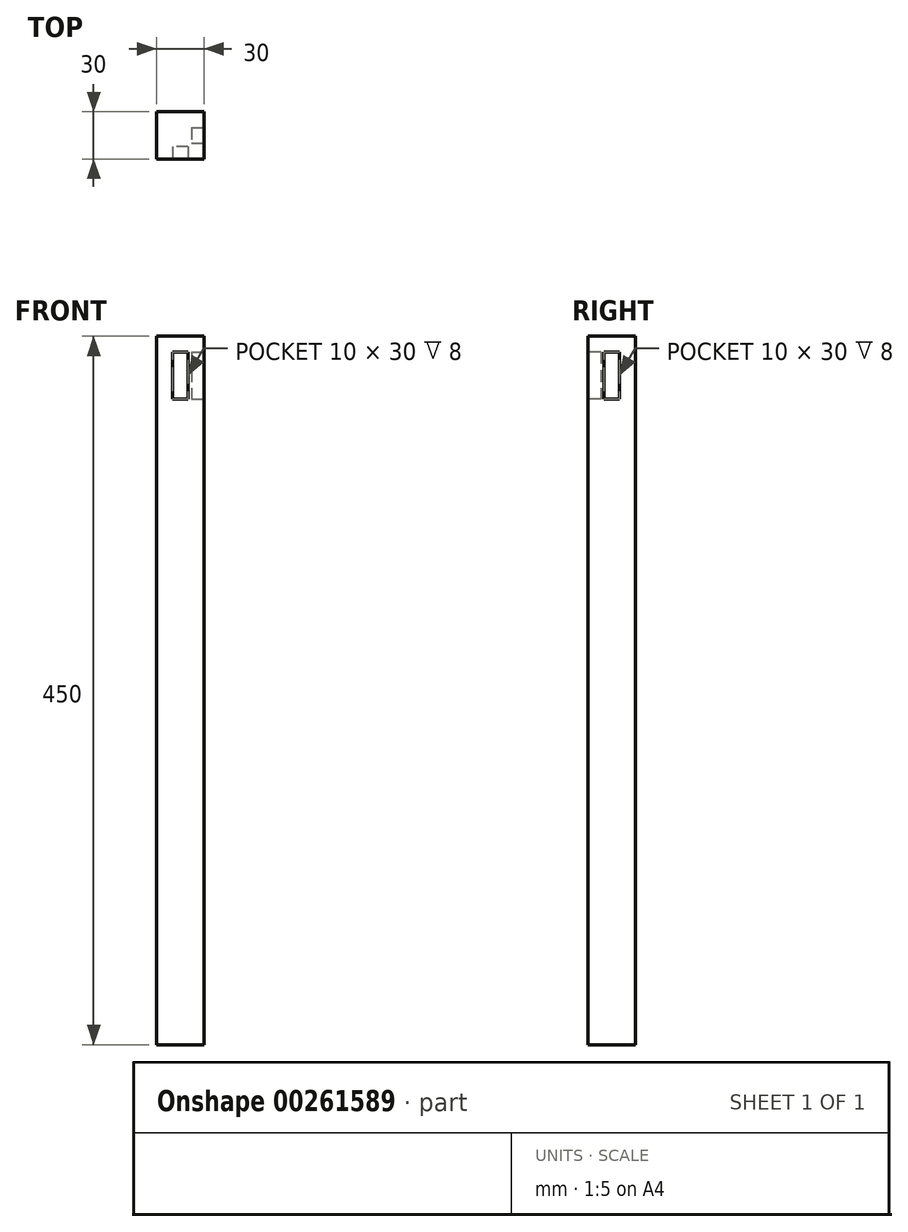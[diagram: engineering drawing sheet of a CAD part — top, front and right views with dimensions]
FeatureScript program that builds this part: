
annotation { "Feature Type Name" : "Feature", "Feature Type Description" : "" }
export const myFeature = defineFeature(function(context is Context, id is Id, definition is map)
    precondition{}
    {
        {
            var Q0;
            Q0=qCreatedBy(makeId("Top.planeOp"),FACE);
            var sketch = newSketch(context, id + "F0", { "sketchPlane" : qUnion([Q0])});
            skLineSegment(sketch, "E0.bottom", {"start": v(0, 0) * mm, "end": v(30, 0) * mm});
            skLineSegment(sketch, "E0.top", {"start": v(0, -30) * mm, "end": v(30, -30) * mm});
            skLineSegment(sketch, "E0.left", {"start": v(0, 0) * mm, "end": v(0, -30) * mm});
            skLineSegment(sketch, "E0.right", {"start": v(30, 0) * mm, "end": v(30, -30) * mm});
            skSolve(sketch);
        }
        {
            var Q0;
            Q0=makeQuery(id+"F0.imprint","IMPRINT",FACE,{"disambiguationData":[TD([[makeQuery(id+"F0.imprint","IMPRINT",EDGE,{"derivedFrom":sQuery(id+"F0.wireOp",EDGE,"E0.bottom")}),-1.0]])]});
            extrude(context, id + "F1", {"entities" : qUnion([Q0]), "depth" : 450 * mm});
        }
        {
            var Q0;
            Q0=makeQuery(id+"F1.opExtrude","SWEPT_FACE",FACE,{"disambiguationData":[OSD([sQuery(id+"F0.wireOp",EDGE,"E0.right")])]});
            var sketch = newSketch(context, id + "F2", { "sketchPlane" : qUnion([Q0])});
            skLineSegment(sketch, "E1.bottom", {"start": v(-10, 440) * mm, "end": v(-20, 440) * mm});
            skLineSegment(sketch, "E1.top", {"start": v(-10, 410) * mm, "end": v(-20, 410) * mm});
            skLineSegment(sketch, "E1.left", {"start": v(-10, 440) * mm, "end": v(-10, 410) * mm});
            skLineSegment(sketch, "E1.right", {"start": v(-20, 440) * mm, "end": v(-20, 410) * mm});
            skSolve(sketch);
        }
        {
            var Q0;
            Q0 = qSketchRegion(id + "F2", true);
            extrude(context, id + "F3", {"entities" : qUnion([Q0]), "operationType" : NewBodyOperationType.REMOVE, "oppositeDirection" : true, "depth" : 8 * mm});
        }
        {
            var Q0;
            Q0=makeQuery(id+"F1.opExtrude","SWEPT_FACE",FACE,{"disambiguationData":[OSD([sQuery(id+"F0.wireOp",EDGE,"E0.top")])]});
            var sketch = newSketch(context, id + "F4", { "sketchPlane" : qUnion([Q0])});
            skLineSegment(sketch, "E2.bottom", {"start": v(20, 440) * mm, "end": v(10, 440) * mm});
            skLineSegment(sketch, "E2.top", {"start": v(20, 410) * mm, "end": v(10, 410) * mm});
            skLineSegment(sketch, "E2.left", {"start": v(20, 440) * mm, "end": v(20, 410) * mm});
            skLineSegment(sketch, "E2.right", {"start": v(10, 440) * mm, "end": v(10, 410) * mm});
            skSolve(sketch);
        }
        {
            var Q0;
            Q0 = qSketchRegion(id + "F4", true);
            extrude(context, id + "F5", {"entities" : qUnion([Q0]), "operationType" : NewBodyOperationType.REMOVE, "oppositeDirection" : true, "depth" : 8 * mm});
        }
    });
